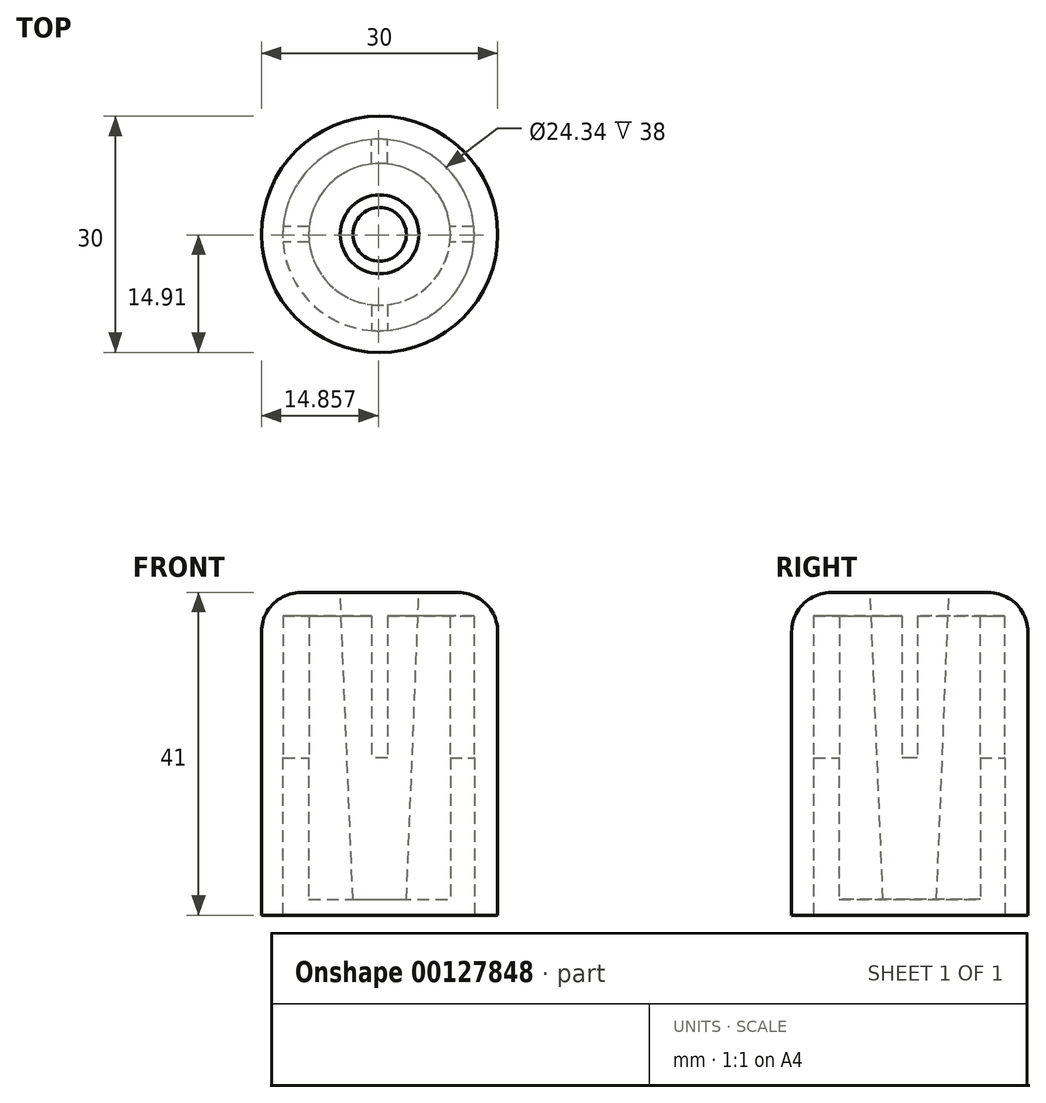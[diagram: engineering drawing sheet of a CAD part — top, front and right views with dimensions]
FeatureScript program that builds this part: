
annotation { "Feature Type Name" : "Feature", "Feature Type Description" : "" }
export const myFeature = defineFeature(function(context is Context, id is Id, definition is map)
    precondition{}
    {
        {
            var Q0;
            Q0=qCreatedBy(makeId("Top.planeOp"),FACE);
            var sketch = newSketch(context, id + "F0", { "sketchPlane" : qUnion([Q0])});
            skCircle(sketch, "E0", {"center": v(0, 0) * mm, "radius": 15 * mm});
            skCircle(sketch, "E1", {"center": v(-0.14, -0.1) * mm, "radius": 12.17 * mm});
            skSolve(sketch);
        }
        {
            var Q0;
            Q0 = qSketchRegion(id + "F0", true);
            extrude(context, id + "F1", {"entities" : qUnion([Q0]), "depth" : 38 * mm});
        }
        {
            var Q0;
            Q0=makeQuery(id+"F1.opExtrude","CAP_FACE",FACE,{"disambiguationData":[OSD([sQuery(id+"F0.wireOp",EDGE,"E0"),sQuery(id+"F0.wireOp",EDGE,"E1")])],"isStart":false});
            var sketch = newSketch(context, id + "F2", { "sketchPlane" : qUnion([Q0])});
            skCircle(sketch, "E2.0", {"center": v(-0.14, -0.1) * mm, "radius": 12.17 * mm});
            skCircle(sketch, "E3.0", {"center": v(0, 0) * mm, "radius": 15 * mm});
            skSolve(sketch);
        }
        {
            var Q0;
            Q0 = qSketchRegion(id + "F2", true);
            var Q1;
            Q1=makeQuery(id+"F2.imprint","IMPRINT",FACE,{"disambiguationData":[TD([[makeQuery(id+"F2.imprint","IMPRINT",EDGE,{"derivedFrom":sQuery(id+"F2.wireOp",EDGE,"E2.0")}),1.0]])]});
            extrude(context, id + "F3", {"entities" : qUnion([Q0, Q1]), "operationType" : NewBodyOperationType.ADD, "depth" : 3 * mm});
        }
        {
            var Q0;
            Q0=makeQuery(id+"F3.opExtrude","CAP_EDGE",EDGE,{"disambiguationData":[OSD([sQuery(id+"F2.wireOp",EDGE,"E3.0")])],"isStart":false});
            fillet(context, id + "F4", {"entities" : qUnion([Q0]), "radius" : 5 * mm, "tangentPropagation" : true, "allowEdgeOverflow" : false});
        }
        {
            var Q0;
            Q0=makeQuery(id+"F3.opExtrude","CAP_FACE",FACE,{"disambiguationData":[OSD([sQuery(id+"F2.wireOp",EDGE,"E3.0")])],"isStart":false});
            var sketch = newSketch(context, id + "F5", { "sketchPlane" : qUnion([Q0])});
            skCircle(sketch, "E4", {"center": v(0, 0) * mm, "radius": 5 * mm});
            skSolve(sketch);
        }
        {
            var Q0;
            Q0 = qSketchRegion(id + "F5", true);
            extrude(context, id + "F6", {"entities" : qUnion([Q0]), "operationType" : NewBodyOperationType.ADD, "oppositeDirection" : true, "depth" : 39 * mm});
        }
        {
            var Q0;
            Q0=makeQuery(id+"F6.opExtrude","CAP_FACE",FACE,{"disambiguationData":[OSD([sQuery(id+"F5.wireOp",EDGE,"E4")])],"isStart":false});
            var sketch = newSketch(context, id + "F7", { "sketchPlane" : qUnion([Q0])});
            skCircle(sketch, "E5", {"center": v(0, 0) * mm, "radius": 3.4 * mm});
            skSolve(sketch);
        }
        {
            var Q1;
            Q1=makeQuery(id+"F5.imprint","IMPRINT",FACE,{"disambiguationData":[TD([[makeQuery(id+"F5.imprint","IMPRINT",EDGE,{"derivedFrom":sQuery(id+"F5.wireOp",EDGE,"E4")}),1.0]])]});
            var Q2;
            Q2=makeQuery(id+"F7.imprint","IMPRINT",FACE,{"disambiguationData":[TD([[makeQuery(id+"F7.imprint","IMPRINT",EDGE,{"derivedFrom":sQuery(id+"F7.wireOp",EDGE,"E5")}),1.0]])]});
            loft(context, id + "F8", {"operationType" : NewBodyOperationType.REMOVE, "sheetProfilesArray" : [{ "sheetProfileEntities" : qUnion([Q1]) }, { "sheetProfileEntities" : qUnion([Q2]) }]});
        }
        {
            var Q0;
            Q0=makeQuery(id+"F6.opExtrude","CAP_FACE",FACE,{"disambiguationData":[OSD([sQuery(id+"F5.wireOp",EDGE,"E4")])],"isStart":false});
            var sketch = newSketch(context, id + "F9", { "sketchPlane" : qUnion([Q0])});
            skCircle(sketch, "E6", {"center": v(0, 0) * mm, "radius": 9 * mm});
            skCircle(sketch, "E7.0", {"center": v(0, 0) * mm, "radius": 5 * mm});
            skSolve(sketch);
        }
        {
            var Q0;
            Q0 = qSketchRegion(id + "F9", true);
            var Q1;
            Q1=makeQuery(id+"F3.opExtrude","CAP_FACE",FACE,{"disambiguationData":[OSD([sQuery(id+"F2.wireOp",EDGE,"E3.0")])],"isStart":true});
            extrude(context, id + "F10", {"entities" : qUnion([Q0]), "operationType" : NewBodyOperationType.ADD, "endBound" : BoundingType.UP_TO_SURFACE, "oppositeDirection" : true, "endBoundEntityFace" : qUnion([Q1]), "depth" : 39 * mm});
        }
        {
            var Q0;
            Q0=qCreatedBy(makeId("Top.planeOp"),FACE);
            cPlane(context, id + "F11", {"entities" : qUnion([Q0]), "cplaneType" : CPlaneType.OFFSET, "offset" : 20 * mm, "width" : 150 * mm, "height" : 150 * mm});
        }
        {
            var Q0;
            Q0=qCreatedBy(id+"F11.planeOp",FACE);
            var sketch = newSketch(context, id + "F12", { "sketchPlane" : qUnion([Q0])});
            skCircle(sketch, "E8.0", {"center": v(-0.14, -0.1) * mm, "radius": 12.17 * mm});
            skLineSegment(sketch, "E9", {"start": v(-12.31, 0) * mm, "end": v(-5, 0) * mm, "construction": true});
            skLineSegment(sketch, "E10", {"start": v(0, -12.26) * mm, "end": v(0, -5) * mm, "construction": true});
            skArc(sketch, "E11.0.startCap", {"start": v(1, -12.26) * mm, "mid": v(0, -13.26) * mm, "end": v(-1, -12.26) * mm});
            skArc(sketch, "E11.0.endCap", {"start": v(-1, 12.08) * mm, "mid": v(0, 13.08) * mm, "end": v(1, 12.08) * mm});
            skLineSegment(sketch, "E11.0.left", {"start": v(-1, -12.26) * mm, "end": v(-1, -4.9) * mm});
            skLineSegment(sketch, "E11.0.right", {"start": v(1, -12.26) * mm, "end": v(1, -4.9) * mm});
            skArc(sketch, "E11.1.startCap", {"start": v(-12.31, -1) * mm, "mid": v(-13.31, 0) * mm, "end": v(-12.31, 1) * mm});
            skArc(sketch, "E11.1.endCap", {"start": v(12.03, 1) * mm, "mid": v(13.03, 0) * mm, "end": v(12.03, -1) * mm});
            skLineSegment(sketch, "E11.1.left", {"start": v(-12.31, 1) * mm, "end": v(-4.9, 1) * mm});
            skLineSegment(sketch, "E11.1.right", {"start": v(-12.31, -1) * mm, "end": v(-4.9, -1) * mm});
            skCircle(sketch, "E12.0.0", {"center": v(0, 0) * mm, "radius": 5 * mm});
            skLineSegment(sketch, "E13.trimOffspring", {"start": v(-1, -1) * mm, "end": v(1, -1) * mm});
            skLineSegment(sketch, "E14.trimOffspring", {"start": v(-1, 0) * mm, "end": v(12.03, 0) * mm, "construction": true});
            skLineSegment(sketch, "E15.trimOffspring", {"start": v(-1, 1) * mm, "end": v(1, 1) * mm});
            skLineSegment(sketch, "E16.trimOffspring", {"start": v(-1, -1) * mm, "end": v(-1, 1) * mm});
            skLineSegment(sketch, "E17.trimOffspring", {"start": v(0, -1) * mm, "end": v(0, 12.08) * mm, "construction": true});
            skLineSegment(sketch, "E18.trimOffspring", {"start": v(1, -1) * mm, "end": v(1, 1) * mm});
            skLineSegment(sketch, "E19.trimOffspring", {"start": v(4.9, -1) * mm, "end": v(12.03, -1) * mm});
            skLineSegment(sketch, "E20.trimOffspring", {"start": v(4.9, 1) * mm, "end": v(12.03, 1) * mm});
            skLineSegment(sketch, "E21.trimOffspring", {"start": v(1, 4.9) * mm, "end": v(1, 12.08) * mm});
            skLineSegment(sketch, "E22.trimOffspring", {"start": v(-1, 4.9) * mm, "end": v(-1, 12.08) * mm});
            skSolve(sketch);
        }
        {
            var Q0;
            {var subQ0=sQuery(id+"F12.wireOp",EDGE,"E11.1.left");var subQ1=sQuery(id+"F12.wireOp",EDGE,"E8.0");var subQ2=makeQuery(id+"F12.imprint","INTERSECT",VERTEX,{"derivedFrom":[subQ1,subQ0]});Q0=makeQuery(id+"F12.imprint","IMPRINT",FACE,{"disambiguationData":[TD([[makeQuery(id+"F12.imprint","IMPRINT",EDGE,{"disambiguationData":[TD([[subQ2,-1.0]])],"derivedFrom":subQ1}),1.0]])]});}
            var Q1;
            {var subQ0=sQuery(id+"F12.wireOp",EDGE,"E20.trimOffspring");var subQ1=sQuery(id+"F12.wireOp",EDGE,"E8.0");var subQ2=makeQuery(id+"F12.imprint","INTERSECT",VERTEX,{"derivedFrom":[subQ1,subQ0]});Q1=makeQuery(id+"F12.imprint","IMPRINT",FACE,{"disambiguationData":[TD([[makeQuery(id+"F12.imprint","IMPRINT",EDGE,{"disambiguationData":[TD([[subQ2,1.0]])],"derivedFrom":subQ1}),1.0]])]});}
            var Q2;
            {var subQ0=sQuery(id+"F12.wireOp",EDGE,"E11.0.left");var subQ1=sQuery(id+"F12.wireOp",EDGE,"E8.0");var subQ2=makeQuery(id+"F12.imprint","INTERSECT",VERTEX,{"derivedFrom":[subQ1,subQ0]});Q2=makeQuery(id+"F12.imprint","IMPRINT",FACE,{"disambiguationData":[TD([[makeQuery(id+"F12.imprint","IMPRINT",EDGE,{"disambiguationData":[TD([[subQ2,-1.0]])],"derivedFrom":subQ1}),1.0]])]});}
            var Q3;
            {var subQ0=sQuery(id+"F12.wireOp",EDGE,"E21.trimOffspring");var subQ1=sQuery(id+"F12.wireOp",EDGE,"E8.0");var subQ2=makeQuery(id+"F12.imprint","INTERSECT",VERTEX,{"derivedFrom":[subQ1,subQ0]});Q3=makeQuery(id+"F12.imprint","IMPRINT",FACE,{"disambiguationData":[TD([[makeQuery(id+"F12.imprint","IMPRINT",EDGE,{"disambiguationData":[TD([[subQ2,-1.0]])],"derivedFrom":subQ1}),1.0]])]});}
            extrude(context, id + "F13", {"entities" : qUnion([Q0, Q1, Q2, Q3]), "operationType" : NewBodyOperationType.ADD, "endBound" : BoundingType.UP_TO_NEXT, "depth" : 25 * mm});
        }
    });
